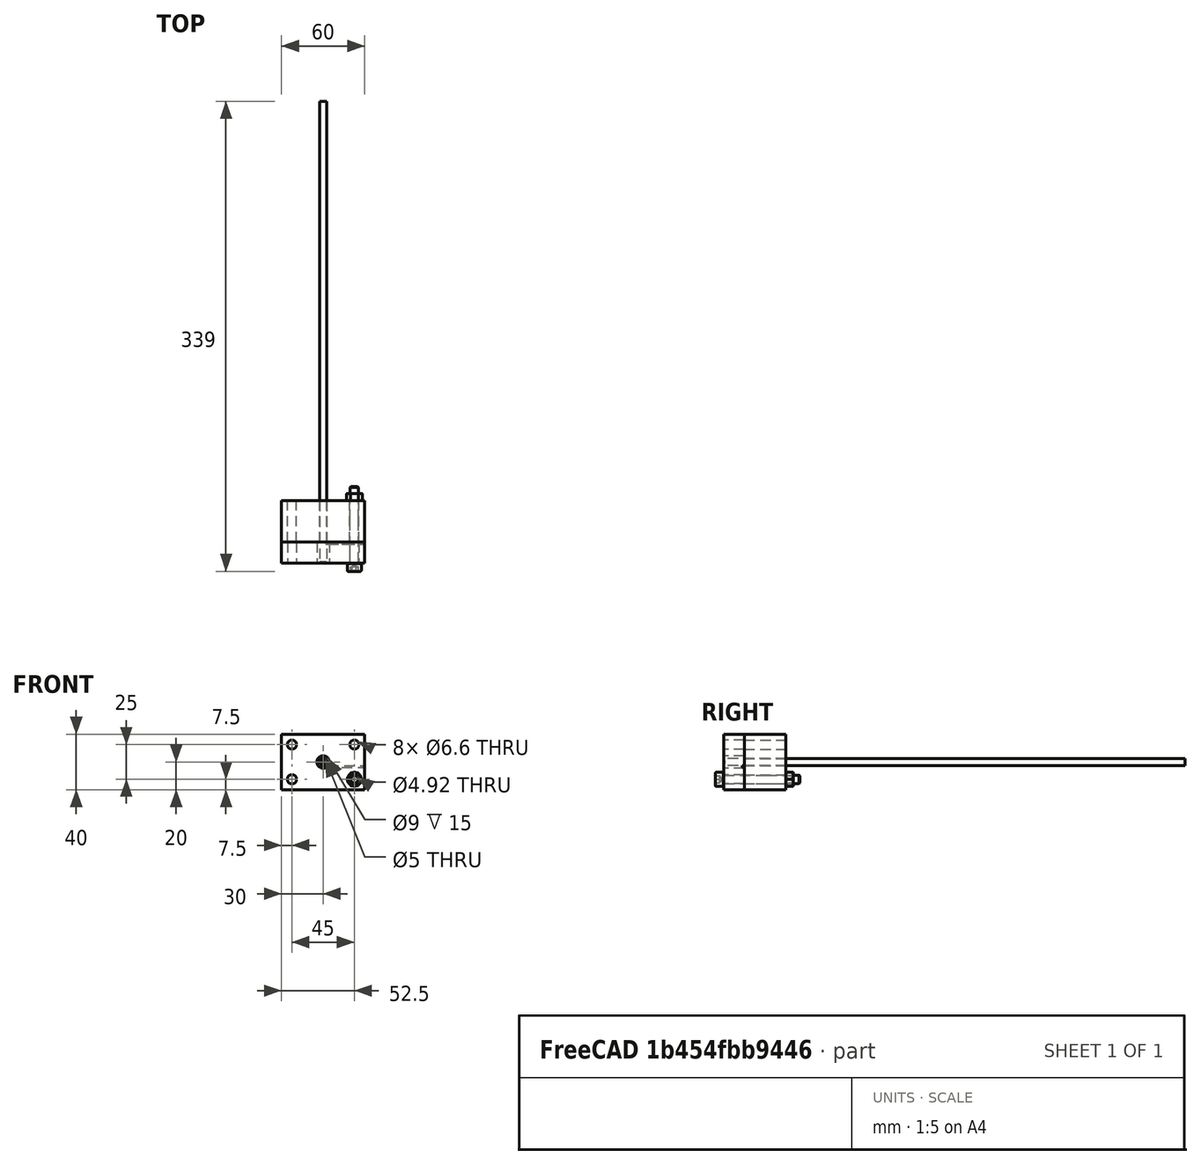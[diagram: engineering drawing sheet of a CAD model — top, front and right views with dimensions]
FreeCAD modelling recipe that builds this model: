
FCSTD DOCUMENT  (FreeCAD 1.0R39319 (Git))
Label: coil winder
License: Creative Commons Attribution 4.0
LicenseURL: https://creativecommons.org/licenses/by/4.0/
objects: Sketcher::SketchObject×9, PartDesign::Hole×4, App::Link×4, App::LinkElement×4, PartDesign::Body×3, PartDesign::Pad×2, PartDesign::SubShapeBinder×2, PartDesign::Pocket×2, App::FeaturePython×2, Part::FeaturePython×2, App::VarSet×1, PartDesign::Revolution×1, Assembly::JointGroup×1, App::Part×1, Assembly::AssemblyObject×1
note: 52 computed .brp shape members not serialized (recipe doc carries the construction recipe); baked Part::Feature solids carry a one-line shape summary decoded from their .brp

FEATURE [App::VarSet] VarSet  label="dims"
  holeSpacingX = 45
  holeSpacingZ = 25
  shaftDiameter = 5
  shaftZ = 20
  wireDiameter = 1.02
FEATURE [Sketcher::SketchObject] Sketch  label="block profile"
  ArcFitTolerance = 1e-06
  AttachmentSupport = -> [XZ_Plane]
  FullyConstrained = true
  MakeInternals = false
  MapMode = 5
  Placement = pos=(0,0,0) rot=(1,0,0;1.5708rad)
  expr: Constraints[11] = <<dims>>.shaftDiameter
  sketch-geometry (7):
    g0: LineSegment StartX=-30 StartY=0 StartZ=0 EndX=30 EndY=0 EndZ=0
    g1: LineSegment StartX=30 StartY=0 StartZ=0 EndX=30 EndY=40 EndZ=0
    g2: LineSegment StartX=30 StartY=40 StartZ=0 EndX=-30 EndY=40 EndZ=0
    g3: LineSegment StartX=-30 StartY=40 StartZ=0 EndX=-30 EndY=0 EndZ=0
    g4: Circle [constr] CenterX=0 CenterY=20 CenterZ=0 NormalX=0 NormalY=0 NormalZ=1 AngleXU=0 Radius=2.5
    g5: LineSegment [constr] StartX=2 StartY=18.5 StartZ=0 EndX=30 EndY=18.5 EndZ=0
    g6: GeomPoint [constr] X=0 Y=17.5 Z=0
  constraints (20):
    c: Coincident(g0,g1)
    c: Coincident(g1,g2)
    c: Coincident(g2,g3)
    c: Coincident(g3,g0)
    c: Horizontal(g2)
    c: Vertical(g1)
    c: Vertical(g3)
    c: PointOnObject(g0,g-1)
    c: PointOnObject(g4,g-2)
    c: PointOnObject(g5,g4)
    c: Horizontal(g5)
    c: Diameter(g4) = 5
    c: PointOnObject(g6,g4)
    c: PointOnObject(g6,g-2)
    c: DistanceY(g6,g5) = 1
    c: DistanceY(g-1,g4) = 20
    c: DistanceY(g3,g3) = 40
    c: DistanceX(g2,g2) = 60
    c: Symmetric(g0,g0,g-2)
    c: PointOnObject(g5,g1)
FEATURE [PartDesign::Pad] Pad
  Direction = (0,-1,2e-16)
  Length = 30
  Length2 = 10
  Placement = pos=(0,0,0) rot=(1,0,0;1.5708rad)
  Profile = -> Sketch
  ReferenceAxis = -> Sketch [N_Axis]
  Refine = true
  Reversed = true
  Suppressed = false
  Type = 0
FEATURE [Sketcher::SketchObject] Sketch001
  ArcFitTolerance = 1e-06
  AttachmentSupport = -> [XZ_Plane]
  FullyConstrained = true
  MakeInternals = false
  MapMode = 5
  Placement = pos=(0,0,0) rot=(1,0,0;1.5708rad)
  expr: Constraints[1] = <<dims>>.shaftDiameter
  expr: Constraints[2] = <<dims>>.shaftZ
  sketch-geometry (1):
    g0: Circle CenterX=0 CenterY=20 CenterZ=0 NormalX=0 NormalY=0 NormalZ=1 AngleXU=0 Radius=2.5
  constraints (3):
    c: PointOnObject(g0,g-2)
    c: Diameter(g0) = 5
    c: DistanceY(g-1,g0) = 20
FEATURE [PartDesign::Hole] Hole  label="shaft bore"
  BaseFeature = -> Pad
  CustomThreadClearance = 0
  Depth = 166.573
  DepthType = 1
  Diameter = 5
  DrillForDepth = false
  DrillPoint = 1
  DrillPointAngle = 118
  HoleCutCountersinkAngle = 90
  HoleCutCustomValues = false
  HoleCutDepth = 0
  HoleCutDiameter = 6.1
  HoleCutType = 0
  ModelThread = false
  Placement = pos=(0,0,0) rot=(1,0,0;1.5708rad)
  Profile = -> Sketch001
  Refine = true
  Suppressed = false
  Tapered = false
  TaperedAngle = 90
  ThreadClass = 0
  ThreadDepth = 166.573
  ThreadDepthType = 0
  ThreadDirection = 0
  ThreadFit = 0
  ThreadSize = 0
  ThreadType = 0
  Threaded = false
  UseCustomThreadClearance = false
  expr: Diameter = <<dims>>.shaftDiameter
FEATURE [PartDesign::SubShapeBinder] Binder  label="rear block binder"
  BindCopyOnChange = 0
  BindMode = 0
  ClaimChildren = false
  Context = -> Body001 [Binder.]
  Fuse = false
  MakeFace = true
  OffsetFill = false
  OffsetIntersection = false
  OffsetJoinType = 0
  OffsetOpenResult = false
  PartialLoad = false
  Refine = true
  Relative = true
  Support = -> [Body[Hole002.]]
  _Version = 2
FEATURE [Sketcher::SketchObject] Sketch002
  ArcFitTolerance = 1e-06
  AttachmentSupport = -> [XZ_Plane001]
  ExternalGeometry = -> [Binder]
  FullyConstrained = true
  MakeInternals = false
  MapMode = 5
  Placement = pos=(0,0,0) rot=(1,0,0;1.5708rad)
  sketch-geometry (4):
    g0: LineSegment StartX=-30 StartY=0 StartZ=0 EndX=30 EndY=0 EndZ=0
    g1: LineSegment StartX=30 StartY=0 StartZ=0 EndX=30 EndY=40 EndZ=0
    g2: LineSegment StartX=30 StartY=40 StartZ=0 EndX=-30 EndY=40 EndZ=0
    g3: LineSegment StartX=-30 StartY=40 StartZ=0 EndX=-30 EndY=0 EndZ=0
  constraints (10):
    c: Coincident(g0,g1)
    c: Coincident(g1,g2)
    c: Coincident(g2,g3)
    c: Coincident(g3,g0)
    c: Horizontal(g2)
    c: Vertical(g1)
    c: Vertical(g3)
    c: PointOnObject(g0,g-1)
    c: Coincident(g2,g-3)
    c: Symmetric(g0,g0,g-2)
FEATURE [PartDesign::Pad] Pad001
  Direction = (0,-1,2e-16)
  Length = 15
  Length2 = 10
  Placement = pos=(0,0,0) rot=(1,0,0;1.5708rad)
  Profile = -> Sketch002
  ReferenceAxis = -> Sketch002 [N_Axis]
  Refine = true
  Suppressed = false
  Type = 0
FEATURE [Sketcher::SketchObject] Sketch003
  ArcFitTolerance = 1e-06
  AttachmentSupport = -> [XZ_Plane001]
  ExternalGeometry = -> [Binder]
  FullyConstrained = true
  MakeInternals = false
  MapMode = 5
  Placement = pos=(0,0,0) rot=(1,0,0;1.5708rad)
  expr: Constraints[0] = <<dims>>.shaftDiameter + 2 * <<dims>>.wireDiameter
  sketch-geometry (1):
    g0: Circle CenterX=0 CenterY=20 CenterZ=0 NormalX=0 NormalY=0 NormalZ=1 AngleXU=0 Radius=3.52
  constraints (2):
    c: Diameter(g0) = 7.04
    c: Coincident(g0,g-3)
FEATURE [PartDesign::Hole] Hole001  label="coil bore"
  BaseFeature = -> Pad001
  CustomThreadClearance = 0
  Depth = 148.782
  DepthType = 1
  Diameter = 9
  DrillForDepth = false
  DrillPoint = 1
  DrillPointAngle = 118
  HoleCutCountersinkAngle = 90
  HoleCutCustomValues = false
  HoleCutDepth = 0
  HoleCutDiameter = 6.1
  HoleCutType = 0
  ModelThread = false
  Placement = pos=(0,0,0) rot=(1,0,0;1.5708rad)
  Profile = -> Sketch003
  Refine = true
  Reversed = true
  Suppressed = false
  Tapered = false
  TaperedAngle = 90
  ThreadClass = 0
  ThreadDepth = 148.782
  ThreadDepthType = 0
  ThreadDirection = 0
  ThreadFit = 0
  ThreadSize = 0
  ThreadType = 0
  Threaded = false
  UseCustomThreadClearance = false
  expr: Diameter = ceil(<<dims>>.shaftDiameter + 2 * <<dims>>.wireDiameter) + 1 mm
FEATURE [Sketcher::SketchObject] Sketch004
  ArcFitTolerance = 1e-06
  AttachmentSupport = -> [YZ_Plane001]
  ExternalGeometry = -> [Hole001]
  FullyConstrained = true
  MakeInternals = false
  MapMode = 5
  Placement = pos=(0,0,0) rot=(0.57735,0.57735,0.57735;2.0944rad)
  expr: Constraints[17] = <<dims>>.shaftDiameter / 2
  expr: Constraints[8] = <<dims>>.wireDiameter + 0.5 mm
  sketch-geometry (8):
    g0: LineSegment StartX=-1.52 StartY=15.98 StartZ=0 EndX=4e-15 EndY=15.98 EndZ=0
    g1: LineSegment StartX=4e-15 StartY=15.98 StartZ=0 EndX=4e-15 EndY=17.5 EndZ=0
    g2: LineSegment StartX=4e-15 StartY=17.5 StartZ=0 EndX=-1.52 EndY=17.5 EndZ=0
    g3: LineSegment StartX=-1.52 StartY=17.5 StartZ=0 EndX=-1.52 EndY=15.98 EndZ=0
    g4: LineSegment [constr] StartX=-1.52 StartY=17.5 StartZ=0 EndX=4e-15 EndY=15.98 EndZ=0
    g5: LineSegment [constr] StartX=-1.52 StartY=15.98 StartZ=0 EndX=4e-15 EndY=17.5 EndZ=0
    g6: GeomPoint [constr] X=-0.76 Y=16.74 Z=0
    g7: GeomPoint [constr] X=4.4e-15 Y=20 Z=0
  constraints (19):
    c: Coincident(g0,g1)
    c: Coincident(g1,g2)
    c: Coincident(g2,g3)
    c: Coincident(g3,g0)
    c: Horizontal(g0)
    c: Horizontal(g2)
    c: Vertical(g1)
    c: Vertical(g3)
    c: DistanceY(g3,g3) = 1.52
    c: Coincident(g4,g2)
    c: Coincident(g4,g0)
    c: Coincident(g5,g0)
    c: Coincident(g5,g1)
    c: PointOnObject(g6,g4)
    c: PointOnObject(g6,g5)
    c: Equal(g3,g0)
    c: Symmetric(g-3,g-3,g7)
    c: DistanceY(g1,g7) = 2.5
    c: PointOnObject(g1,g-3)
FEATURE [PartDesign::Pocket] Pocket  label="wire insert groove"
  BaseFeature = -> Hole001
  Direction = (-1,0,0)
  Length = 5
  Length2 = 5
  Placement = pos=(0,0,0) rot=(1,0,0;1.5708rad)
  Profile = -> Sketch004
  ReferenceAxis = -> Sketch004 [N_Axis]
  Refine = true
  Reversed = true
  Suppressed = false
  Type = 1
FEATURE [Sketcher::SketchObject] Sketch005
  ArcFitTolerance = 1e-06
  AttachmentSupport = -> [XZ_Plane]
  ExternalGeometry = -> [Hole]
  FullyConstrained = true
  MakeInternals = false
  MapMode = 5
  Placement = pos=(0,0,0) rot=(1,0,0;1.5708rad)
  expr: Constraints[17] = <<dims>>.holeSpacingX
  expr: Constraints[18] = <<dims>>.holeSpacingZ
  sketch-geometry (9):
    g0: Circle CenterX=-22.5 CenterY=32.5 CenterZ=0 NormalX=0 NormalY=0 NormalZ=1 AngleXU=0 Radius=3
    g1: Circle CenterX=22.5 CenterY=7.5 CenterZ=0 NormalX=0 NormalY=0 NormalZ=1 AngleXU=0 Radius=3
    g2: Circle CenterX=22.5 CenterY=32.5 CenterZ=0 NormalX=0 NormalY=0 NormalZ=1 AngleXU=0 Radius=3
    g3: Circle CenterX=-22.5 CenterY=7.5 CenterZ=0 NormalX=0 NormalY=0 NormalZ=1 AngleXU=0 Radius=3
    g4: LineSegment [constr] StartX=-22.5 StartY=7.5 StartZ=0 EndX=22.5 EndY=7.5 EndZ=0
    g5: LineSegment [constr] StartX=22.5 StartY=7.5 StartZ=0 EndX=22.5 EndY=32.5 EndZ=0
    g6: LineSegment [constr] StartX=22.5 StartY=32.5 StartZ=0 EndX=-22.5 EndY=32.5 EndZ=0
    g7: LineSegment [constr] StartX=-22.5 StartY=32.5 StartZ=0 EndX=-22.5 EndY=7.5 EndZ=0
    g8: GeomPoint [constr] X=-1e-16 Y=20 Z=0
  constraints (20):
    c: Equal(g0,g2)
    c: Equal(g2,g1)
    c: Equal(g1,g3)
    c: Coincident(g4,g5)
    c: Coincident(g5,g6)
    c: Coincident(g6,g7)
    c: Coincident(g7,g4)
    c: Horizontal(g4)
    c: Horizontal(g6)
    c: Vertical(g5)
    c: Vertical(g7)
    c: Symmetric(g6,g4,g8)
    c: Coincident(g8,g-3)
    c: Coincident(g5,g2)
    c: Coincident(g4,g3)
    c: Coincident(g0,g6)
    c: Coincident(g1,g4)
    c: DistanceX(g6,g6) = 45
    c: DistanceY(g7,g7) = 25
    c: Diameter(g0) = 6
FEATURE [PartDesign::Hole] Hole002  label="bolt holes"
  BaseFeature = -> Hole
  CustomThreadClearance = 0
  Depth = 166.573
  DepthType = 1
  Diameter = 6.6
  DrillForDepth = false
  DrillPoint = 1
  DrillPointAngle = 118
  HoleCutCountersinkAngle = 90
  HoleCutCustomValues = false
  HoleCutDepth = 0
  HoleCutDiameter = 0
  HoleCutType = 0
  ModelThread = false
  Placement = pos=(0,0,0) rot=(1,0,0;1.5708rad)
  Profile = -> Sketch005
  Refine = true
  Suppressed = false
  Tapered = false
  TaperedAngle = 90
  ThreadClass = 0
  ThreadDepth = 166.573
  ThreadDepthType = 0
  ThreadDirection = 0
  ThreadFit = 0
  ThreadSize = 14
  ThreadType = 1
  Threaded = false
  UseCustomThreadClearance = false
FEATURE [PartDesign::Body] Body  label="OCT-CWRBL-AA"
  AllowCompound = false
  Group = -> [Sketch,Pad,Sketch001,Hole,Sketch005,Hole002]
  Origin = -> Origin
  Tip = -> Hole002
FEATURE [Sketcher::SketchObject] Sketch006
  ArcFitTolerance = 1e-06
  AttachmentSupport = -> [XZ_Plane001]
  FullyConstrained = true
  MakeInternals = false
  MapMode = 5
  Placement = pos=(0,0,0) rot=(1,0,0;1.5708rad)
  expr: Constraints[18] = <<dims>>.holeSpacingX
  expr: Constraints[19] = <<dims>>.holeSpacingZ
  expr: Constraints[20] = <<dims>>.shaftZ
  sketch-geometry (9):
    g0: LineSegment [constr] StartX=-22.5 StartY=7.5 StartZ=0 EndX=22.5 EndY=7.5 EndZ=0
    g1: LineSegment [constr] StartX=22.5 StartY=7.5 StartZ=0 EndX=22.5 EndY=32.5 EndZ=0
    g2: LineSegment [constr] StartX=22.5 StartY=32.5 StartZ=0 EndX=-22.5 EndY=32.5 EndZ=0
    g3: LineSegment [constr] StartX=-22.5 StartY=32.5 StartZ=0 EndX=-22.5 EndY=7.5 EndZ=0
    g4: GeomPoint [constr] X=0 Y=20 Z=0
    g5: Circle CenterX=-22.5 CenterY=32.5 CenterZ=0 NormalX=0 NormalY=0 NormalZ=1 AngleXU=0 Radius=3
    g6: Circle CenterX=22.5 CenterY=32.5 CenterZ=0 NormalX=0 NormalY=0 NormalZ=1 AngleXU=0 Radius=3
    g7: Circle CenterX=22.5 CenterY=7.5 CenterZ=0 NormalX=0 NormalY=0 NormalZ=1 AngleXU=0 Radius=3
    g8: Circle CenterX=-22.5 CenterY=7.5 CenterZ=0 NormalX=0 NormalY=0 NormalZ=1 AngleXU=0 Radius=3
  constraints (21):
    c: Coincident(g0,g1)
    c: Coincident(g1,g2)
    c: Coincident(g2,g3)
    c: Coincident(g3,g0)
    c: Horizontal(g0)
    c: Horizontal(g2)
    c: Vertical(g1)
    c: Vertical(g3)
    c: Symmetric(g2,g0,g4)
    c: PointOnObject(g4,g-2)
    c: Coincident(g5,g2)
    c: Coincident(g6,g1)
    c: Coincident(g7,g0)
    c: Coincident(g8,g0)
    c: Equal(g8,g5)
    c: Equal(g5,g6)
    c: Equal(g6,g7)
    c: Diameter(g5) = 6
    c: DistanceX(g2,g2) = 45
    c: DistanceY(g3,g3) = 25
    c: DistanceY(g-1,g4) = 20
FEATURE [PartDesign::Hole] Hole003  label="bolt holes"
  BaseFeature = -> Pocket
  CustomThreadClearance = 0
  Depth = 148.782
  DepthType = 1
  Diameter = 6.6
  DrillForDepth = false
  DrillPoint = 1
  DrillPointAngle = 118
  HoleCutCountersinkAngle = 90
  HoleCutCustomValues = false
  HoleCutDepth = 0
  HoleCutDiameter = 6.1
  HoleCutType = 0
  ModelThread = false
  Placement = pos=(0,0,0) rot=(1,0,0;1.5708rad)
  Profile = -> Sketch006
  Refine = true
  Reversed = true
  Suppressed = false
  Tapered = false
  TaperedAngle = 90
  ThreadClass = 0
  ThreadDepth = 148.782
  ThreadDepthType = 0
  ThreadDirection = 0
  ThreadFit = 0
  ThreadSize = 14
  ThreadType = 1
  Threaded = false
  UseCustomThreadClearance = false
FEATURE [PartDesign::Body] Body001  label="OCT-CWFBL-AA"
  AllowCompound = false
  Group = -> [Binder,Sketch002,Pad001,Sketch003,Hole001,Sketch004,Pocket,Sketch006,Hole003]
  Origin = -> Origin001
  Tip = -> Hole003
FEATURE [PartDesign::SubShapeBinder] Binder001
  BindCopyOnChange = 0
  BindMode = 0
  ClaimChildren = false
  Context = -> Body002 [Binder001.]
  Fuse = false
  MakeFace = true
  OffsetFill = false
  OffsetIntersection = false
  OffsetJoinType = 0
  OffsetOpenResult = false
  PartialLoad = false
  Refine = true
  Relative = true
  Support = -> [Body[Hole002.Face5],Body001[Hole003.Face5]]
  _Version = 2
FEATURE [Sketcher::SketchObject] Sketch007
  ArcFitTolerance = 1e-06
  AttachmentSupport = -> [YZ_Plane002]
  ExternalGeometry = -> [Binder001]
  FullyConstrained = true
  MakeInternals = false
  MapMode = 5
  Placement = pos=(0,0,0) rot=(0.57735,0.57735,0.57735;2.0944rad)
  expr: Constraints[8] = <<dims>>.shaftZ
  expr: Constraints[9] = <<dims>>.shaftDiameter / 2
  sketch-geometry (4):
    g0: LineSegment StartX=-15 StartY=20 StartZ=0 EndX=318 EndY=20 EndZ=0
    g1: LineSegment StartX=318 StartY=20 StartZ=0 EndX=318 EndY=22.5 EndZ=0
    g2: LineSegment StartX=318 StartY=22.5 StartZ=0 EndX=-15 EndY=22.5 EndZ=0
    g3: LineSegment StartX=-15 StartY=22.5 StartZ=0 EndX=-15 EndY=20 EndZ=0
  constraints (12):
    c: Coincident(g0,g1)
    c: Coincident(g1,g2)
    c: Coincident(g2,g3)
    c: Coincident(g3,g0)
    c: Horizontal(g0)
    c: Horizontal(g2)
    c: Vertical(g1)
    c: Vertical(g3)
    c: DistanceY(g-1,g0) = 20
    c: DistanceY(g3,g3) = 2.5
    c: Vertical(g2,g-3)
    c: DistanceX(g2,g2) = 333
FEATURE [PartDesign::Revolution] Revolution
  Angle = 360
  Angle2 = 60
  Axis = (0,1,0)
  Base = (0,-15,20)
  Placement = pos=(0,0,0) rot=(1,1,1;2.0944rad)
  Profile = -> Sketch007
  ReferenceAxis = -> Sketch007 [Edge1]
  Refine = true
  Reversed = true
  Suppressed = false
  Type = 0
FEATURE [Sketcher::SketchObject] Sketch008
  ArcFitTolerance = 1e-06
  AttachmentSupport = -> [YZ_Plane002]
  ExternalGeometry = -> [Binder001]
  FullyConstrained = true
  MakeInternals = false
  MapMode = 5
  Placement = pos=(0,0,0) rot=(0.57735,0.57735,0.57735;2.0944rad)
  expr: Constraints[11] = <<dims>>.shaftZ
  expr: Constraints[8] = <<dims>>.wireDiameter + 1 mm
  expr: Constraints[9] = <<dims>>.wireDiameter
  sketch-geometry (5):
    g0: LineSegment StartX=-15 StartY=21.01 StartZ=0 EndX=-15 EndY=18.99 EndZ=0
    g1: LineSegment StartX=-15 StartY=18.99 StartZ=0 EndX=-13.98 EndY=18.99 EndZ=0
    g2: LineSegment StartX=-13.98 StartY=18.99 StartZ=0 EndX=-13.98 EndY=21.01 EndZ=0
    g3: LineSegment StartX=-13.98 StartY=21.01 StartZ=0 EndX=-15 EndY=21.01 EndZ=0
    g4: GeomPoint X=-15 Y=20 Z=0
  constraints (13):
    c: Coincident(g0,g1)
    c: Coincident(g1,g2)
    c: Coincident(g2,g3)
    c: Coincident(g3,g0)
    c: Vertical(g0)
    c: Vertical(g2)
    c: Horizontal(g1)
    c: Horizontal(g3)
    c: DistanceY(g0,g0) = 2.02
    c: DistanceX(g1,g1) = 1.02
    c: Symmetric(g0,g0,g4)
    c: DistanceY(g-1,g4) = 20
    c: Vertical(g0,g-3)
FEATURE [PartDesign::Pocket] Pocket001
  BaseFeature = -> Revolution
  Direction = (-1,0,0)
  Length = 5
  Length2 = 5
  Midplane = true
  Placement = pos=(0,0,0) rot=(1,1,1;2.0944rad)
  Profile = -> Sketch008
  ReferenceAxis = -> Sketch008 [N_Axis]
  Refine = true
  Suppressed = false
  Type = 1
FEATURE [PartDesign::Body] Body002  label="OCT-CWSFT-AA"
  AllowCompound = false
  Group = -> [Binder001,Sketch007,Revolution,Sketch008,Pocket001]
  Origin = -> Origin002
  Tip = -> Pocket001
FEATURE [App::Link] OCT_CWRBL_AA  label="OCT-CWRBL-AA"
  LinkedObject = -> Body
FEATURE [App::FeaturePython] GroundedJoint  # Assembly grounded joint (typed FeaturePython)
  ObjectToGround = -> OCT_CWRBL_AA
FEATURE [App::Link] OCT_CWFBL_AA  label="OCT-CWFBL-AA"
  LinkPlacement = pos=(-1.42e-14,-6.7e-15,0) rot=(0,0,1;0rad)
  LinkedObject = -> Body001
  Placement = pos=(-1.42e-14,-6.7e-15,0) rot=(0,0,1;0rad)
FEATURE [App::Link] OCT_CWSFT_AA  label="OCT-CWSFT-AA"
  LinkPlacement = pos=(-2.0337,-38.3542,0.103667) rot=(0,1,0;0.101861rad)
  LinkedObject = -> Body002
  Placement = pos=(-2.0337,-38.3542,0.103667) rot=(0,1,0;0.101861rad)
FEATURE [App::FeaturePython] Joint001  label="Cylindrical"  # Assembly joint (typed FeaturePython)
  Activated = true
  AngleMax = 0
  AngleMin = 0
  Detach1 = false
  Detach2 = false
  Distance = 0
  Distance2 = 0
  EnableAngleMax = false
  EnableAngleMin = false
  EnableLengthMax = false
  EnableLengthMin = false
  JointType = 2 (Cylindrical)
  LengthMax = 0
  LengthMin = 0
  Placement1 = pos=(-1.29e-14,-13.98,20) rot=(0.57735,-0.57735,0.57735;2.0944rad)
  Placement2 = pos=(0,30,20) rot=(1,0,0;1.5708rad)
  Reference1 = -> Assembly [OCT_CWSFT_AA.Face2,OCT_CWSFT_AA.Edge4]
  Reference2 = -> Assembly [OCT_CWRBL_AA.Face10,OCT_CWRBL_AA.Edge2]
FEATURE [Assembly::JointGroup] Joints
  Group = -> [GroundedJoint,Joint001]
FEATURE [Part::FeaturePython] Screw  label="M6x55-Screw"  # WARN: FeaturePython — macro-defined, semantics opaque (R4)
  BaseObject = -> OCT_CWFBL_AA [Hole003.Edge27]
  Diameter = 7
  Invert = false
  LeftHanded = false
  Length = 12
  LengthCustom = 55
  MatchOuter = false
  OffsetAngle = 0
  Placement = pos=(22.5,-15,7.5) rot=(1,0,0;1.5708rad)
  Thread = false
  Type = 75
FEATURE [Part::FeaturePython] Nut  label="M6-Nut"  # WARN: FeaturePython — macro-defined, semantics opaque (R4)
  BaseObject = -> OCT_CWRBL_AA [Hole002.Edge20]
  Diameter = 8
  Invert = false
  LeftHanded = false
  MatchOuter = false
  OffsetAngle = 0
  Placement = pos=(22.5,30,7.5) rot=(-1,0,0;1.5708rad)
  Thread = false
  Type = 31
FEATURE [App::Part] Part  label="block fasteners"
  Group = -> [Nut,Screw]
  Origin = -> Origin004
FEATURE [App::LinkElement] Link_i0
  LinkedObject = -> Part
  _LinkOwner = 86
FEATURE [App::LinkElement] Link_i1
  LinkPlacement = pos=(0,0,25) rot=(0,0,1;0rad)
  LinkedObject = -> Part
  Placement = pos=(0,0,25) rot=(0,0,1;0rad)
  _LinkOwner = 86
  expr: .Placement.Base.z = <<dims>>.holeSpacingZ
FEATURE [App::LinkElement] Link_i2
  LinkPlacement = pos=(-45,0,0) rot=(0,0,1;0rad)
  LinkedObject = -> Part
  Placement = pos=(-45,0,0) rot=(0,0,1;0rad)
  _LinkOwner = 86
  expr: .Placement.Base.x = -<<dims>>.holeSpacingX
FEATURE [App::LinkElement] Link_i3
  LinkPlacement = pos=(-45,0,25) rot=(0,0,1;0rad)
  LinkedObject = -> Part
  Placement = pos=(-45,0,25) rot=(0,0,1;0rad)
  _LinkOwner = 86
  expr: .Placement.Base.x = -<<dims>>.holeSpacingX
  expr: .Placement.Base.z = <<dims>>.holeSpacingZ
FEATURE [App::Link] Link  label="block fasteners"
  ElementCount = 4
  ElementList = -> [Link_i0,Link_i1,Link_i2,Link_i3]
  LinkedObject = -> Part
FEATURE [Assembly::AssemblyObject] Assembly  label="Coil Winder"
  Group = -> [Joints,OCT_CWRBL_AA,GroundedJoint,OCT_CWFBL_AA,OCT_CWSFT_AA,Joint001,Link]
  Origin = -> Origin003
  Type = Assembly
